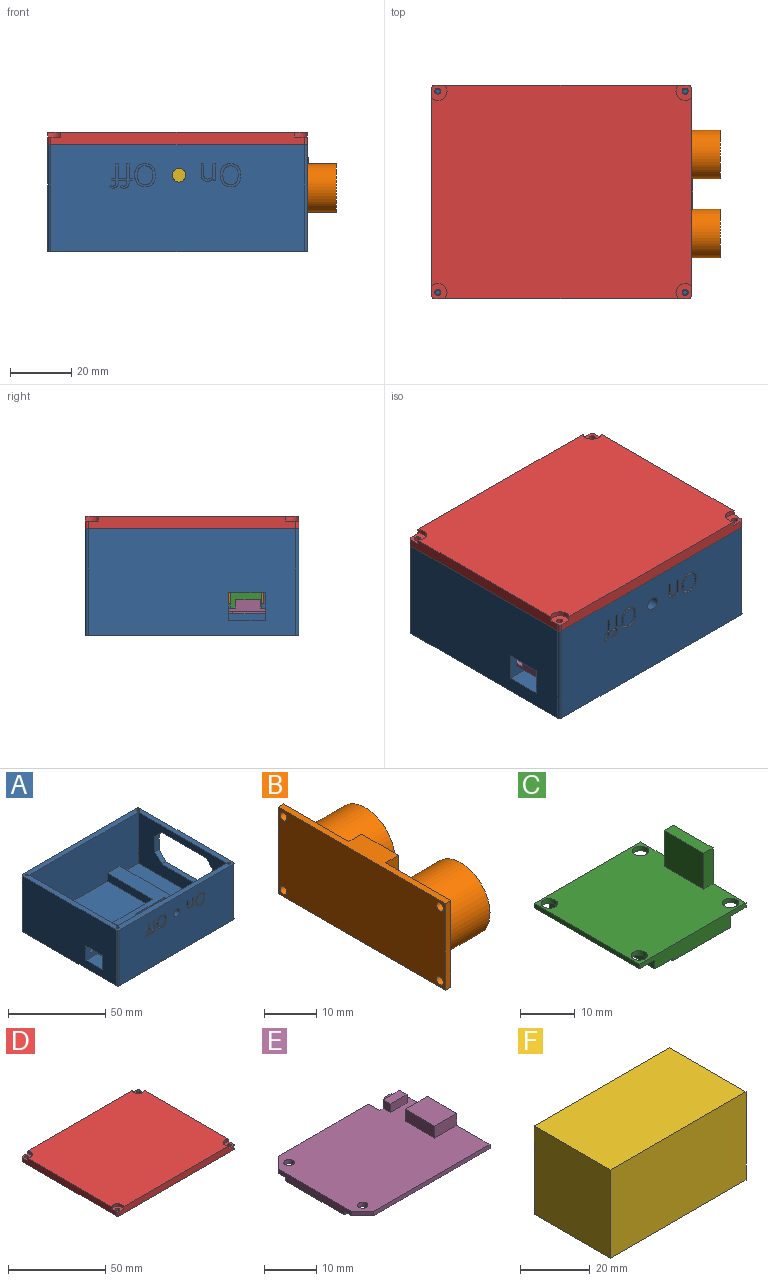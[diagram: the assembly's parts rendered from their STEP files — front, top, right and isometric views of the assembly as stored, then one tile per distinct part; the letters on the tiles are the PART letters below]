
ASSEMBLY  parts=6 mates=5
PART A: 160 faces, bbox 85x70x35 mm
  f0: plane 64x56.5mm, normal (0,0,1), area 2563mm2, adj f1,f5,f7,f11,f17,f129,f130,f159
  f1: plane 29x5mm, normal (0,1,0), area 145mm2, adj f0,f5,f6,f159
  f2: plane 85x70mm, normal (0,0,-1), area 5445.1mm2, adj f9,f12,f13,f16,f18,f19,f20,f21
  f3: plane 28x28mm, normal (0,0,1), area 364mm2, adj f7,f136,f141,f142,f143,f144,f145,f146
  f4: plane 6x3.5mm, normal (0,0,1), area 21mm2, adj f7,f136,f146,f147
  f5: plane 31x5mm, normal (-1,0,0), area 107mm2, adj f0,f1,f6,f7,f137,f138,f140
  f6: plane 64x38mm, normal (0,0,1), area 626mm2, adj f1,f5,f7,f17,f136,f137,f138,f139
  f7: plane 79x32mm, normal (0,1,0), area 2347.1mm2, adj f0,f3,f4,f5,f6,f8,f10,f11
  f8: plane 64x13.5mm, normal (0,0,1), area 864mm2, adj f7,f14,f17,f136
  f9: plane 68x35mm, normal (-1,0,0), area 2272mm2, adj f2,f15,f18,f19,f132,f133,f134,f135
  f10: plane 8x5.5mm, normal (0,0,1), area 44mm2, adj f7,f11,f130,f133
  f11: plane 64x32mm, normal (1,0,0), area 1836mm2, adj f0,f7,f10,f15,f17,f129,f131,f132
  f12: plane 83x35mm, normal (0,-1,0), area 2774.1mm2, adj f2,f15,f19,f20,f38,f39,f40,f41
  f13: plane 68x35mm, normal (1,0,0), area 1590mm2, adj f2,f15,f20,f21,f30,f31,f32,f33
  f14: plane 64x32mm, normal (-1,0,0), area 1258mm2, adj f7,f8,f15,f17,f30,f31,f32,f33
  f15: plane 85x70mm, normal (0,0,1), area 886.1mm2, adj f7,f9,f11,f12,f13,f14,f16,f17
  f16: plane 83x35mm, normal (0,1,0), area 2905mm2, adj f2,f15,f18,f21
  f17: plane 79x32mm, normal (0,-1,0), area 2483mm2, adj f0,f6,f8,f11,f14,f15,f136,f159
  f18: cylinder r=1mm len=35mm, axis (0,0,1), area 55mm2, adj f2,f9,f15,f16
  f19: cylinder r=1mm len=35mm, axis (0,0,-1), area 55mm2, adj f2,f9,f12,f15
  f20: cylinder r=1mm len=35mm, axis (0,0,1), area 55mm2, adj f2,f12,f13,f15
  f21: cylinder r=1mm len=35mm, axis (0,0,-1), area 55mm2, adj f2,f13,f15,f16
  f22: cylinder r=0.75mm len=10mm, axis (0,0,1), area 47.1mm2, adj f15,f23
  f23: plane 1.5x1.5mm, normal (0,0,1), area 1.8mm2, adj f22
  f24: cylinder r=0.75mm len=10mm, axis (0,0,1), area 47.1mm2, adj f15,f25
  f25: plane 1.5x1.5mm, normal (0,0,1), area 1.8mm2, adj f24
  f26: cylinder r=0.75mm len=10mm, axis (0,0,1), area 47.1mm2, adj f15,f27
  f27: plane 1.5x1.5mm, normal (0,0,1), area 1.8mm2, adj f26
  f28: cylinder r=0.75mm len=10mm, axis (0,0,1), area 47.1mm2, adj f15,f29
  f29: plane 1.5x1.5mm, normal (0,0,1), area 1.8mm2, adj f28
  f30: plane 32x3mm, normal (0,0,-1), area 96mm2, adj f13,f14,f36,f37
  f31: plane 10x3mm, normal (0,-1,0), area 30mm2, adj f13,f14,f35,f37
  f32: plane 32x3mm, normal (0,0,1), area 96mm2, adj f13,f14,f34,f35
  f33: plane 10x3mm, normal (0,1,0), area 30mm2, adj f13,f14,f34,f36
  f34: plane 5x5mm, normal (0,0.71,0.71), area 21.2mm2, adj f13,f14,f32,f33
  f35: plane 5x5mm, normal (0,-0.71,0.71), area 21.2mm2, adj f13,f14,f31,f32
  f36: plane 5x5mm, normal (0,0.71,-0.71), area 21.2mm2, adj f13,f14,f30,f33
  f37: plane 5x5mm, normal (0,-0.71,-0.71), area 21.2mm2, adj f13,f14,f30,f31
  f38: cylinder r=2.25mm len=4.5mm, axis (0,1,0), area 42.4mm2, adj f7,f12
  f39: plane 1.5x1.42mm, normal (0,0,-1), area 2.1mm2, adj f12,f40,f55,f56
  f40: plane 1.5x0.66mm, normal (1,0,0), area 1mm2, adj f12,f39,f41,f56
  f41: plane 1.5x1.42mm, normal (0,0,1), area 2.1mm2, adj f12,f40,f42,f56
  f42: plane 1.5x0.36mm, normal (1,0,0), area 0.5mm2, adj f12,f41,f43,f56
  f43: extruded ~1.5x1.02mm, area 1.6mm2, adj f12,f42,f44,f56
  f44: extruded ~1.5x0.71mm, area 1.2mm2, adj f12,f43,f45,f56
  f45: extruded ~1.5x0.83mm, area 1.3mm2, adj f12,f44,f46,f56
  f46: plane 1.5x0.68mm, normal (0.95,0,-0.31), area 1.1mm2, adj f12,f45,f47,f56
  f47: extruded ~1.5x1.04mm, area 1.6mm2, adj f12,f46,f48,f56
  f48: extruded ~2.05x1.79mm, area 4.7mm2, adj f12,f47,f49,f56
  f49: plane 1.5x0.31mm, normal (-1,0,0), area 0.5mm2, adj f12,f48,f50,f56
  f50: plane 1.5x0.99mm, normal (-0.29,0,0.96), area 1.6mm2, adj f12,f49,f51,f56
  f51: plane 1.5x0.38mm, normal (-1,0,0), area 0.6mm2, adj f12,f50,f52,f56
  f52: plane 1.5x0.99mm, normal (0,0,-1), area 1.5mm2, adj f12,f51,f53,f56
  f53: plane 4.91x1.5mm, normal (-1,0,0), area 7.4mm2, adj f12,f52,f54,f56
  f54: plane 1.5x0.84mm, normal (0,0,-1), area 1.3mm2, adj f12,f53,f55,f56
  f55: plane 4.91x1.5mm, normal (1,0,0), area 7.4mm2, adj f12,f39,f54,f56
  f56: plane 7.96x3.82mm, normal (0,-1,0), area 9.1mm2, adj f39,f40,f41,f42,f43,f44,f45,f46
  f57: extruded ~2.29x1.5mm, area 3.6mm2, adj f58,f72,f73,f127
  f58: extruded ~2.27x1.5mm, area 3.6mm2, adj f57,f59,f73,f127
  f59: extruded ~1.88x1.5mm, area 3.2mm2, adj f58,f60,f73,f127
  f60: extruded ~1.86x1.5mm, area 3.1mm2, adj f59,f61,f73,f127
  f61: extruded ~2.27x1.5mm, area 3.6mm2, adj f60,f62,f73,f127
  f62: extruded ~2.29x1.5mm, area 3.6mm2, adj f61,f63,f73,f127
  f63: extruded ~1.86x1.5mm, area 3.1mm2, adj f62,f72,f73,f127
  f64: extruded ~2.8x1.5mm, area 4.5mm2, adj f12,f65,f71,f73
  f65: extruded ~2.8x1.5mm, area 4.5mm2, adj f12,f64,f66,f73
  f66: extruded ~2.5x1.5mm, area 4.2mm2, adj f12,f65,f67,f73
  f67: extruded ~2.54x1.5mm, area 4.2mm2, adj f12,f66,f68,f73
  f68: extruded ~2.81x1.5mm, area 4.5mm2, adj f12,f67,f69,f73
  f69: extruded ~2.83x1.5mm, area 4.6mm2, adj f12,f68,f70,f73
  f70: extruded ~2.53x1.5mm, area 4.2mm2, adj f12,f69,f71,f73
  f71: extruded ~2.51x1.5mm, area 4.2mm2, adj f12,f64,f70,f73
  f72: extruded ~1.87x1.5mm, area 3.1mm2, adj f57,f63,f73,f127
  f73: plane 7.64x6.83mm, normal (0,-1,0), area 17.4mm2, adj f57,f58,f59,f60,f61,f62,f63,f64
  f74: extruded ~2.29x1.5mm, area 3.6mm2, adj f75,f89,f90,f128
  f75: extruded ~2.27x1.5mm, area 3.6mm2, adj f74,f76,f90,f128
  f76: extruded ~1.88x1.5mm, area 3.2mm2, adj f75,f77,f90,f128
  f77: extruded ~1.86x1.5mm, area 3.1mm2, adj f76,f78,f90,f128
  f78: extruded ~2.27x1.5mm, area 3.6mm2, adj f77,f79,f90,f128
  f79: extruded ~2.29x1.5mm, area 3.6mm2, adj f78,f80,f90,f128
  f80: extruded ~1.86x1.5mm, area 3.1mm2, adj f79,f89,f90,f128
  f81: extruded ~2.8x1.5mm, area 4.5mm2, adj f12,f82,f88,f90
  f82: extruded ~2.8x1.5mm, area 4.5mm2, adj f12,f81,f83,f90
  f83: extruded ~2.5x1.5mm, area 4.2mm2, adj f12,f82,f84,f90
  f84: extruded ~2.54x1.5mm, area 4.2mm2, adj f12,f83,f85,f90
  f85: extruded ~2.81x1.5mm, area 4.5mm2, adj f12,f84,f86,f90
  f86: extruded ~2.83x1.5mm, area 4.6mm2, adj f12,f85,f87,f90
  f87: extruded ~2.53x1.5mm, area 4.2mm2, adj f12,f86,f88,f90
  f88: extruded ~2.51x1.5mm, area 4.2mm2, adj f12,f81,f87,f90
  f89: extruded ~1.87x1.5mm, area 3.1mm2, adj f74,f80,f90,f128
  f90: plane 7.64x6.83mm, normal (0,-1,0), area 17.4mm2, adj f74,f75,f76,f77,f78,f79,f80,f81
  f91: plane 3.6x1.5mm, normal (-1,0,0), area 5.4mm2, adj f12,f92,f107,f108
  f92: plane 1.5x0.84mm, normal (0,0,-1), area 1.3mm2, adj f12,f91,f93,f108
  f93: plane 3.63x1.5mm, normal (1,0,0), area 5.4mm2, adj f12,f92,f94,f108
  f94: extruded ~1.55x1.5mm, area 2.5mm2, adj f12,f93,f95,f108
  f95: extruded ~1.51x1.5mm, area 2.4mm2, adj f12,f94,f96,f108
  f96: extruded ~1.5x1.04mm, area 1.6mm2, adj f12,f95,f97,f108
  f97: extruded ~1.5x0.73mm, area 1.5mm2, adj f12,f96,f98,f108
  f98: plane 1.5x0.04mm, normal (0,0,1), area 0.1mm2, adj f12,f97,f99,f108
  f99: plane 1.5x0.76mm, normal (0.98,0,0.18), area 1.2mm2, adj f12,f98,f100,f108
  f100: plane 1.5x0.69mm, normal (0,0,1), area 1mm2, adj f12,f99,f101,f108
  f101: plane 5.57x1.5mm, normal (-1,0,0), area 8.3mm2, adj f12,f100,f102,f108
  f102: plane 1.5x0.84mm, normal (0,0,-1), area 1.3mm2, adj f12,f101,f103,f108
  f103: plane 2.92x1.5mm, normal (1,0,0), area 4.4mm2, adj f12,f102,f104,f108
  f104: extruded ~1.56x1.5mm, area 2.5mm2, adj f12,f103,f105,f108
  f105: extruded ~1.5x1.28mm, area 2.1mm2, adj f12,f104,f106,f108
  f106: extruded ~1.5x0.97mm, area 1.6mm2, adj f12,f105,f107,f108
  f107: extruded ~1.5x1.01mm, area 1.6mm2, adj f12,f91,f106,f108
  f108: plane 5.67x4.65mm, normal (0,-1,0), area 11.2mm2, adj f91,f92,f93,f94,f95,f96,f97,f98
  f109: plane 1.5x1.42mm, normal (0,0,-1), area 2.1mm2, adj f12,f110,f125,f126
  f110: plane 1.5x0.66mm, normal (1,0,0), area 1mm2, adj f12,f109,f111,f126
  f111: plane 1.5x1.42mm, normal (0,0,1), area 2.1mm2, adj f12,f110,f112,f126
  f112: plane 1.5x0.36mm, normal (1,0,0), area 0.5mm2, adj f12,f111,f113,f126
  f113: extruded ~1.5x1.02mm, area 1.6mm2, adj f12,f112,f114,f126
  f114: extruded ~1.5x0.71mm, area 1.2mm2, adj f12,f113,f115,f126
  f115: extruded ~1.5x0.83mm, area 1.3mm2, adj f12,f114,f116,f126
  f116: plane 1.5x0.68mm, normal (0.95,0,-0.31), area 1.1mm2, adj f12,f115,f117,f126
  f117: extruded ~1.5x1.04mm, area 1.6mm2, adj f12,f116,f118,f126
  f118: extruded ~2.05x1.79mm, area 4.7mm2, adj f12,f117,f119,f126
  f119: plane 1.5x0.31mm, normal (-1,0,0), area 0.5mm2, adj f12,f118,f120,f126
  f120: plane 1.5x0.99mm, normal (-0.29,0,0.96), area 1.6mm2, adj f12,f119,f121,f126
  f121: plane 1.5x0.38mm, normal (-1,0,0), area 0.6mm2, adj f12,f120,f122,f126
  f122: plane 1.5x0.99mm, normal (0,0,-1), area 1.5mm2, adj f12,f121,f123,f126
  f123: plane 4.91x1.5mm, normal (-1,0,0), area 7.4mm2, adj f12,f122,f124,f126
  f124: plane 1.5x0.84mm, normal (0,0,-1), area 1.3mm2, adj f12,f123,f125,f126
  f125: plane 4.91x1.5mm, normal (1,0,0), area 7.4mm2, adj f12,f109,f124,f126
  f126: plane 7.96x3.82mm, normal (0,-1,0), area 9.1mm2, adj f109,f110,f111,f112,f113,f114,f115,f116
  f127: plane 6.11x5mm, normal (0,-1,0), area 25.4mm2, adj f57,f58,f59,f60,f61,f62,f63,f72
  f128: plane 6.11x5mm, normal (0,-1,0), area 25.4mm2, adj f74,f75,f76,f77,f78,f79,f80,f89
  f129: plane 5.5x5mm, normal (0,1,0), area 27.5mm2, adj f0,f11,f130,f131
  f130: plane 28x5mm, normal (1,0,0), area 104mm2, adj f0,f7,f10,f129,f131,f132,f133,f134
  f131: plane 8x5.5mm, normal (0,0,1), area 44mm2, adj f11,f129,f130,f132
  f132: plane 9x8.5mm, normal (0,-1,0), area 43.5mm2, adj f9,f11,f130,f131,f134,f135
  f133: plane 9x8.5mm, normal (0,1,0), area 43.5mm2, adj f9,f10,f11,f130,f134,f135
  f134: plane 12x8.5mm, normal (0,0,1), area 102mm2, adj f9,f130,f132,f133
  f135: plane 12x3mm, normal (0,0,-1), area 36mm2, adj f9,f11,f132,f133
  f136: plane 64x5mm, normal (1,0,0), area 280mm2, adj f3,f4,f6,f7,f8,f17,f147,f148
  f137: plane 8x3mm, normal (0,-1,0), area 24mm2, adj f5,f6,f139,f140
  f138: plane 8x3mm, normal (0,1,0), area 24mm2, adj f5,f6,f139,f140
  f139: plane 16x3mm, normal (-1,0,0), area 48mm2, adj f6,f137,f138,f140
  f140: plane 16x8mm, normal (0,0,1), area 128mm2, adj f5,f137,f138,f139
  f141: plane 6x2.5mm, normal (1,0,0), area 15mm2, adj f3,f6,f142,f158
  f142: plane 3.5x2.5mm, normal (0,-1,0), area 8.8mm2, adj f3,f6,f141,f143
  f143: plane 16x2.5mm, normal (1,0,0), area 40mm2, adj f3,f6,f142,f144
  f144: plane 3.5x2.5mm, normal (0,1,0), area 8.8mm2, adj f3,f6,f143,f145
  f145: plane 6x2.5mm, normal (1,0,0), area 15mm2, adj f3,f6,f7,f144
  f146: plane 6x2.5mm, normal (-1,0,0), area 15mm2, adj f3,f4,f7,f147
  f147: plane 3.5x2.5mm, normal (0,1,0), area 8.8mm2, adj f3,f4,f136,f146
  f148: plane 3.5x2.5mm, normal (0,-1,0), area 8.8mm2, adj f3,f6,f136,f149
  f149: plane 6x2.5mm, normal (-1,0,0), area 15mm2, adj f3,f6,f148,f158
  f150: plane 14x3.5mm, normal (0,-1,0), area 49mm2, adj f3,f151,f153,f155
  f151: plane 24x3.5mm, normal (1,0,0), area 84mm2, adj f3,f150,f152,f154
  f152: plane 14x3.5mm, normal (0,1,0), area 49mm2, adj f3,f151,f153,f156
  f153: plane 24x3.5mm, normal (-1,0,0), area 84mm2, adj f3,f150,f152,f157
  f154: plane 28x2mm, normal (0.71,0,-0.71), area 73.5mm2, adj f2,f151,f155,f156
  f155: plane 18x2mm, normal (0,-0.71,-0.71), area 45.3mm2, adj f2,f150,f154,f157
  f156: plane 18x2mm, normal (0,0.71,-0.71), area 45.3mm2, adj f2,f152,f154,f157
  f157: plane 28x2mm, normal (-0.71,0,-0.71), area 73.5mm2, adj f2,f153,f155,f156
  f158: plane 21x2.5mm, normal (0,-1,0), area 52.5mm2, adj f3,f6,f141,f149
  f159: plane 33x5mm, normal (-1,0,0), area 165mm2, adj f0,f1,f6,f17
PART B: 18 faces, bbox 14x45.5x20.4 mm
  f0: plane 45.5x20.4mm, normal (1,0,0), area 469.7mm2, adj f1,f2,f3,f4,f6,f7,f8,f9
  f1: plane 20.4x1.5mm, normal (0,1,0), area 30.6mm2, adj f0,f2,f4,f5
  f2: plane 45.5x5mm, normal (0,0,1), area 103.3mm2, adj f0,f1,f3,f5,f14,f15,f17
  f3: plane 20.4x1.5mm, normal (0,-1,0), area 30.6mm2, adj f0,f2,f4,f5
  f4: plane 45.5x1.5mm, normal (0,0,-1), area 68.2mm2, adj f0,f1,f3,f5
  f5: plane 45.5x20.4mm, normal (-1,0,0), area 916.9mm2, adj f1,f2,f3,f4,f6,f7,f8,f9
  f6: cylinder r=0.95mm len=1.9mm, axis (1,0,0), area 9mm2, adj f0,f5
  f7: cylinder r=0.95mm len=1.9mm, axis (1,0,0), area 9mm2, adj f0,f5
  f8: cylinder r=0.95mm len=1.9mm, axis (1,0,0), area 9mm2, adj f0,f5
  f9: cylinder r=0.95mm len=1.9mm, axis (1,0,0), area 9mm2, adj f0,f5
  f10: cylinder r=7.95mm len=15.9mm, axis (-1,0,0), area 624.4mm2, adj f0,f11
  f11: plane 15.9x15.9mm, normal (1,0,0), area 198.6mm2, adj f10
  f12: cylinder r=7.95mm len=15.9mm, axis (-1,0,0), area 624.4mm2, adj f0,f13
  f13: plane 15.9x15.9mm, normal (1,0,0), area 198.6mm2, adj f12
  f14: plane 5x3.5mm, normal (0,1,0), area 17.5mm2, adj f0,f2,f16,f17
  f15: plane 5x3.5mm, normal (0,-1,0), area 17.5mm2, adj f0,f2,f16,f17
  f16: plane 10x3.5mm, normal (0,0,-1), area 35mm2, adj f0,f14,f15,f17
  f17: plane 10x5mm, normal (1,0,0), area 50mm2, adj f2,f14,f15,f16
PART C: 24 faces, bbox 27.5x27.2x11.5 mm
  f0: plane 27.2x4.5mm, normal (0,0,-1), area 122.4mm2, adj f3,f5,f21,f22
  f1: plane 27.2x4mm, normal (0,0,-1), area 74.3mm2, adj f3,f5,f6,f12,f13,f16,f17,f18
  f2: plane 27.5x27.2mm, normal (0,0,1), area 695.2mm2, adj f3,f4,f5,f6,f8,f9,f10,f12
  f3: plane 27.5x3.5mm, normal (0,1,0), area 74mm2, adj f0,f1,f2,f4,f6,f7,f20,f21
  f4: plane 27.2x1mm, normal (-1,0,0), area 27.2mm2, adj f2,f3,f5,f7
  f5: plane 27.5x3.5mm, normal (0,-1,0), area 74mm2, adj f0,f1,f2,f4,f6,f7,f20,f21
  f6: plane 27.2x11mm, normal (1,0,0), area 129.2mm2, adj f1,f2,f3,f5,f8,f10,f11,f16
  f7: plane 27.2x4mm, normal (0,0,-1), area 94.7mm2, adj f3,f4,f5,f14,f15,f21
  f8: plane 8x2.4mm, normal (0,1,0), area 19.2mm2, adj f2,f6,f9,f11
  f9: plane 10.2x8mm, normal (-1,0,0), area 81.6mm2, adj f2,f8,f10,f11
  f10: plane 8x2.4mm, normal (0,-1,0), area 19.2mm2, adj f2,f6,f9,f11
  f11: plane 10.2x2.4mm, normal (0,0,1), area 24.5mm2, adj f6,f8,f9,f10
  f12: cylinder r=1.5mm len=3mm, axis (0,0,1), area 9.4mm2, adj f1,f2
  f13: cylinder r=1.5mm len=3mm, axis (0,0,1), area 9.4mm2, adj f1,f2
  f14: cylinder r=1.5mm len=3mm, axis (0,0,1), area 9.4mm2, adj f2,f7
  f15: cylinder r=1.5mm len=3mm, axis (0,0,1), area 9.4mm2, adj f2,f7
  f16: plane 2x2mm, normal (0,1,0), area 4mm2, adj f1,f6,f18,f19
  f17: plane 2x2mm, normal (0,-1,0), area 4mm2, adj f1,f6,f18,f19
  f18: plane 10.2x2mm, normal (-1,0,0), area 20.4mm2, adj f1,f16,f17,f19
  f19: plane 10.2x2mm, normal (0,0,-1), area 20.4mm2, adj f6,f16,f17,f18
  f20: plane 27.2x2.5mm, normal (1,0,0), area 68mm2, adj f1,f3,f5,f23
  f21: plane 27.2x2mm, normal (-1,0,0), area 54.4mm2, adj f0,f3,f5,f7
  f22: plane 27.2x0.5mm, normal (-1,0,0), area 13.6mm2, adj f0,f3,f5,f23
  f23: plane 27.2x15mm, normal (0,0,-1), area 408mm2, adj f3,f5,f20,f22
PART D: 22 faces, bbox 85x70x4 mm
  f0: cylinder r=1mm len=2.5mm, axis (0,0,1), area 3.9mm2, adj f4,f5,f9,f17
  f1: cylinder r=1mm len=2.5mm, axis (0,0,-1), area 3.9mm2, adj f5,f6,f9,f15
  f2: cylinder r=1mm len=2.5mm, axis (0,0,1), area 3.9mm2, adj f6,f7,f9,f13
  f3: cylinder r=1mm len=2.5mm, axis (0,0,-1), area 3.9mm2, adj f4,f7,f9,f11
  f4: plane 83x4mm, normal (0,1,0), area 322.3mm2, adj f0,f3,f8,f9,f10,f11,f16,f17
  f5: plane 68x4mm, normal (-1,0,0), area 262.3mm2, adj f0,f1,f8,f9,f14,f15,f16,f17
  f6: plane 83x4mm, normal (0,-1,0), area 322.3mm2, adj f1,f2,f8,f9,f12,f13,f14,f15
  f7: plane 68x4mm, normal (1,0,0), area 262.3mm2, adj f2,f3,f8,f9,f10,f11,f12,f13
  f8: plane 85x70mm, normal (0,0,1), area 5861.6mm2, adj f4,f5,f6,f7,f10,f12,f14,f16
  f9: plane 85x70mm, normal (0,0,-1), area 5936.6mm2, adj f0,f1,f2,f3,f4,f5,f6,f7
  f10: cylinder r=3mm len=5mm, axis (0,0,1), area 13.6mm2, adj f4,f7,f8,f11
  f11: plane 5x5mm, normal (0,0,1), area 18.8mm2, adj f3,f4,f7,f10,f21
  f12: cylinder r=3mm len=5mm, axis (0,0,1), area 13.6mm2, adj f6,f7,f8,f13
  f13: plane 5x5mm, normal (0,0,1), area 18.8mm2, adj f2,f6,f7,f12,f20
  f14: cylinder r=3mm len=5mm, axis (0,0,1), area 13.6mm2, adj f5,f6,f8,f15
  f15: plane 5x5mm, normal (0,0,1), area 18.8mm2, adj f1,f5,f6,f14,f19
  f16: cylinder r=3mm len=5mm, axis (0,0,1), area 13.6mm2, adj f4,f5,f8,f17
  f17: plane 5x5mm, normal (0,0,1), area 18.8mm2, adj f0,f4,f5,f16,f18
  f18: cylinder r=1mm len=2.5mm, axis (0,0,1), area 15.7mm2, adj f9,f17
  f19: cylinder r=1mm len=2.5mm, axis (0,0,1), area 15.7mm2, adj f9,f15
  f20: cylinder r=1mm len=2.5mm, axis (0,0,1), area 15.7mm2, adj f9,f13
  f21: cylinder r=1mm len=2.5mm, axis (0,0,1), area 15.7mm2, adj f9,f11
PART E: 33 faces, bbox 34.5x26x4.6 mm
  f0: plane 34.5x26mm, normal (0,0,-1), area 758.7mm2, adj f2,f3,f4,f5,f6,f7,f8,f9
  f1: plane 34.5x26mm, normal (0,0,1), area 803.7mm2, adj f2,f3,f4,f5,f6,f7,f8,f9
  f2: plane 23x3.8mm, normal (1,0,0), area 45.4mm2, adj f0,f1,f5,f10,f11,f13,f14
  f3: plane 24.5x1mm, normal (0,1,0), area 24.5mm2, adj f0,f1,f6,f15
  f4: plane 20x1.8mm, normal (-1,0,0), area 32.8mm2, adj f0,f1,f6,f7,f25,f27,f28
  f5: plane 31.5x1mm, normal (0,-1,0), area 31.5mm2, adj f0,f1,f2,f7
  f6: plane 3x3mm, normal (-0.71,0.71,0), area 4.2mm2, adj f0,f1,f3,f4
  f7: plane 3x3mm, normal (-0.71,-0.71,0), area 4.2mm2, adj f0,f1,f4,f5
  f8: cylinder r=1mm len=2mm, axis (0,0,1), area 6.3mm2, adj f0,f1
  f9: cylinder r=1mm len=2mm, axis (0,0,1), area 6.3mm2, adj f0,f1
  f10: plane 6x2.8mm, normal (0,-1,0), area 16.8mm2, adj f1,f2,f12,f13
  f11: plane 6x2.8mm, normal (0,1,0), area 16.8mm2, adj f1,f2,f12,f13
  f12: plane 8x2.8mm, normal (-1,0,0), area 22.4mm2, adj f1,f10,f11,f13
  f13: plane 8x6mm, normal (0,0,1), area 48mm2, adj f2,f10,f11,f12
  f14: plane 7x3mm, normal (0,1,0), area 14mm2, adj f0,f1,f2,f15,f16,f17,f19,f20
  f15: plane 3x1mm, normal (1,0,0), area 3mm2, adj f0,f1,f3,f14
  f16: plane 2x2mm, normal (1,0,0), area 4mm2, adj f1,f14,f18,f19
  f17: plane 2x2mm, normal (-1,0,0), area 4mm2, adj f1,f14,f18,f19
  f18: plane 4.5x2mm, normal (0,-1,0), area 9mm2, adj f1,f16,f17,f19
  f19: plane 4.5x2mm, normal (0,0,1), area 9mm2, adj f14,f16,f17,f18
  f20: plane 1.8x1mm, normal (0,0,1), area 1.8mm2, adj f14,f21,f23,f24
  f21: plane 1.1x1mm, normal (1,0,0), area 1.1mm2, adj f14,f20,f22,f24
  f22: plane 1.8x1mm, normal (0,0,-1), area 1.8mm2, adj f14,f21,f23,f24
  f23: plane 1.1x1mm, normal (-1,0,0), area 1.1mm2, adj f14,f20,f22,f24
  f24: plane 1.8x1.1mm, normal (0,1,0), area 1.8mm2, adj f20,f21,f22,f23,f29
  f25: plane 6x0.8mm, normal (0,1,0), area 4.8mm2, adj f0,f4,f26,f28
  f26: plane 13x0.8mm, normal (1,0,0), area 10.4mm2, adj f0,f25,f28,f31
  f27: plane 8x0.8mm, normal (0,-1,0), area 6.4mm2, adj f0,f4,f28,f32
  f28: plane 16x8mm, normal (0,0,-1), area 102mm2, adj f4,f25,f26,f27,f31,f32
  f29: cylinder r=0.25mm len=0.5mm, axis (0,-1,0), area 0.2mm2, adj f24,f30
  f30: plane 0.5x0.5mm, normal (0,1,0), area 0.2mm2, adj f29
  f31: plane 2x0.8mm, normal (0,1,0), area 1.6mm2, adj f0,f26,f28,f32
  f32: plane 3x0.8mm, normal (1,0,0), area 2.4mm2, adj f0,f27,f28,f31
PART F: 6 faces, bbox 55x31x31 mm
  f0: plane 55x31mm, normal (0,1,0), area 1705mm2, adj f1,f3,f4,f5
  f1: plane 31x31mm, normal (-1,0,0), area 961mm2, adj f0,f2,f4,f5
  f2: plane 55x31mm, normal (0,-1,0), area 1705mm2, adj f1,f3,f4,f5
  f3: plane 31x31mm, normal (1,0,0), area 961mm2, adj f0,f2,f4,f5
  f4: plane 55x31mm, normal (0,0,1), area 1705mm2, adj f0,f1,f2,f3
  f5: plane 55x31mm, normal (0,0,-1), area 1705mm2, adj f0,f1,f2,f3
PLACE A t=(-22.87,-41.49,-76.41)mm
PLACE B t=(11.44,-49.56,-47.9)mm
PLACE C rot(axis=(-0.69,0,0.72),0deg) t=(-22.84,-57.09,-68.41)mm
PLACE D t=(-19.06,-27.57,-41.41)mm
PLACE E rot(axis=(0,0,-1),180deg) t=(-20.13,-79.32,-68.41)mm
PLACE F t=(-54.28,-30.37,-73.41)mm
MATE planar C.f7 <-> A.f4  axis (0,0,-1) through (-26.17,-58.16,-68.41)mm
MATE planar B.f0 <-> A.f14  axis (1,0,0) through (12.94,-41.26,-56.48)mm
MATE planar E.f0 <-> A.f131  axis (0,0,-1) through (-50.21,-58.67,-68.41)mm
MATE planar F.f5 <-> A.f8  axis (0,0,-1) through (-37.97,-25.11,-73.41)mm
MATE fastened D.f14 <-> A.f28  axis (0,0,1) through (-67.06,-73.57,-41.41)mm
